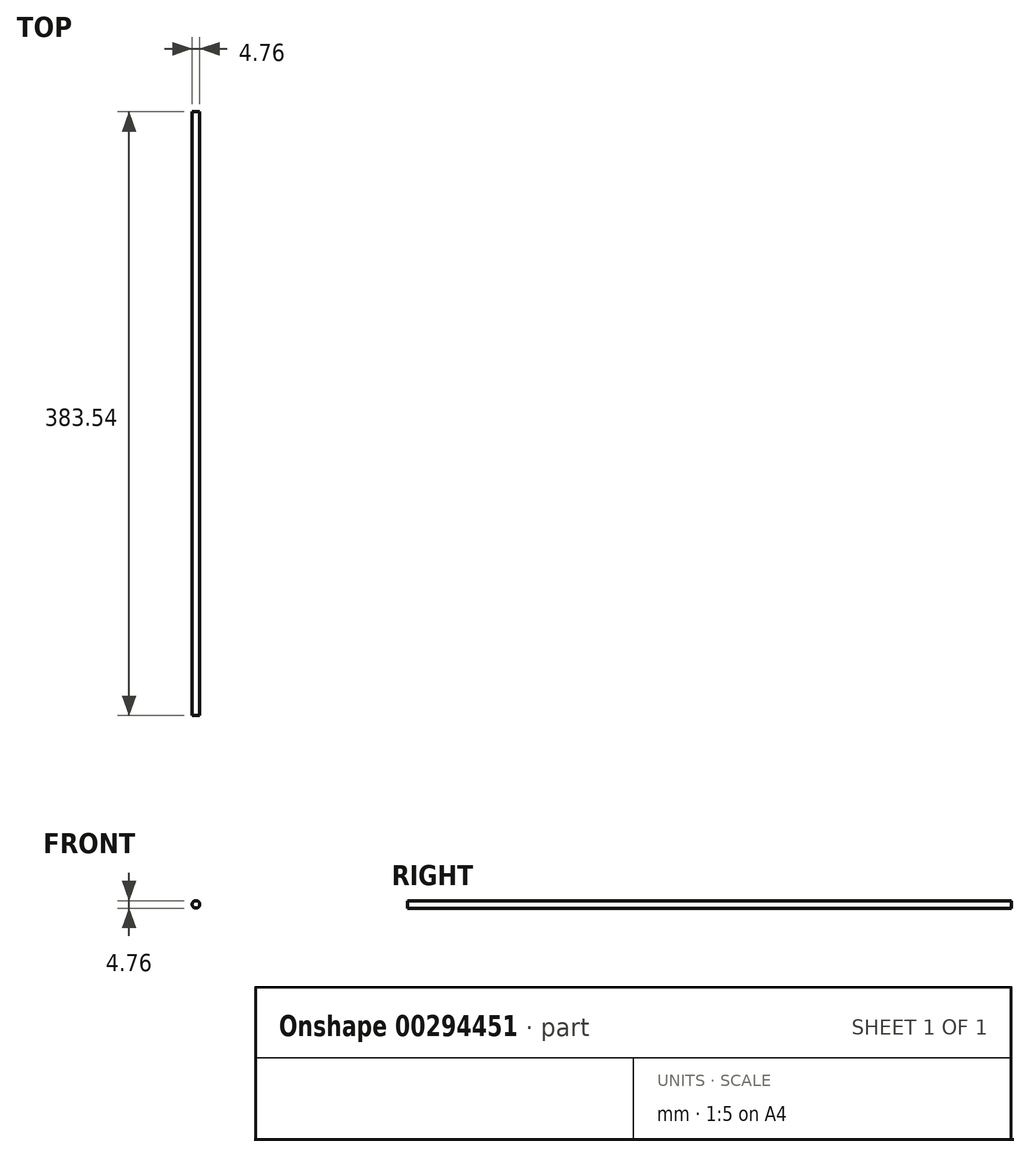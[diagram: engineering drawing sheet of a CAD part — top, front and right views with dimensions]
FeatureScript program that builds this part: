
annotation { "Feature Type Name" : "Feature", "Feature Type Description" : "" }
export const myFeature = defineFeature(function(context is Context, id is Id, definition is map)
    precondition{}
    {
        {
            var Q0;
            Q0=qCreatedBy(makeId("Front.planeOp"),FACE);
            var sketch = newSketch(context, id + "F0", { "sketchPlane" : qUnion([Q0])});
            skCircle(sketch, "E0", {"center": v(0, 0) * mm, "radius": 2.38 * mm});
            skSolve(sketch);
        }
        {
            var Q0;
            Q0=makeQuery(id+"F0.imprint","IMPRINT",FACE,{"disambiguationData":[TD([[makeQuery(id+"F0.imprint","IMPRINT",EDGE,{"derivedFrom":sQuery(id+"F0.wireOp",EDGE,"E0")}),1.0]])]});
            extrude(context, id + "F1", {"entities" : qUnion([Q0]), "endBound" : BoundingType.SYMMETRIC, "depth" : 383.54 * mm});
        }
    });
